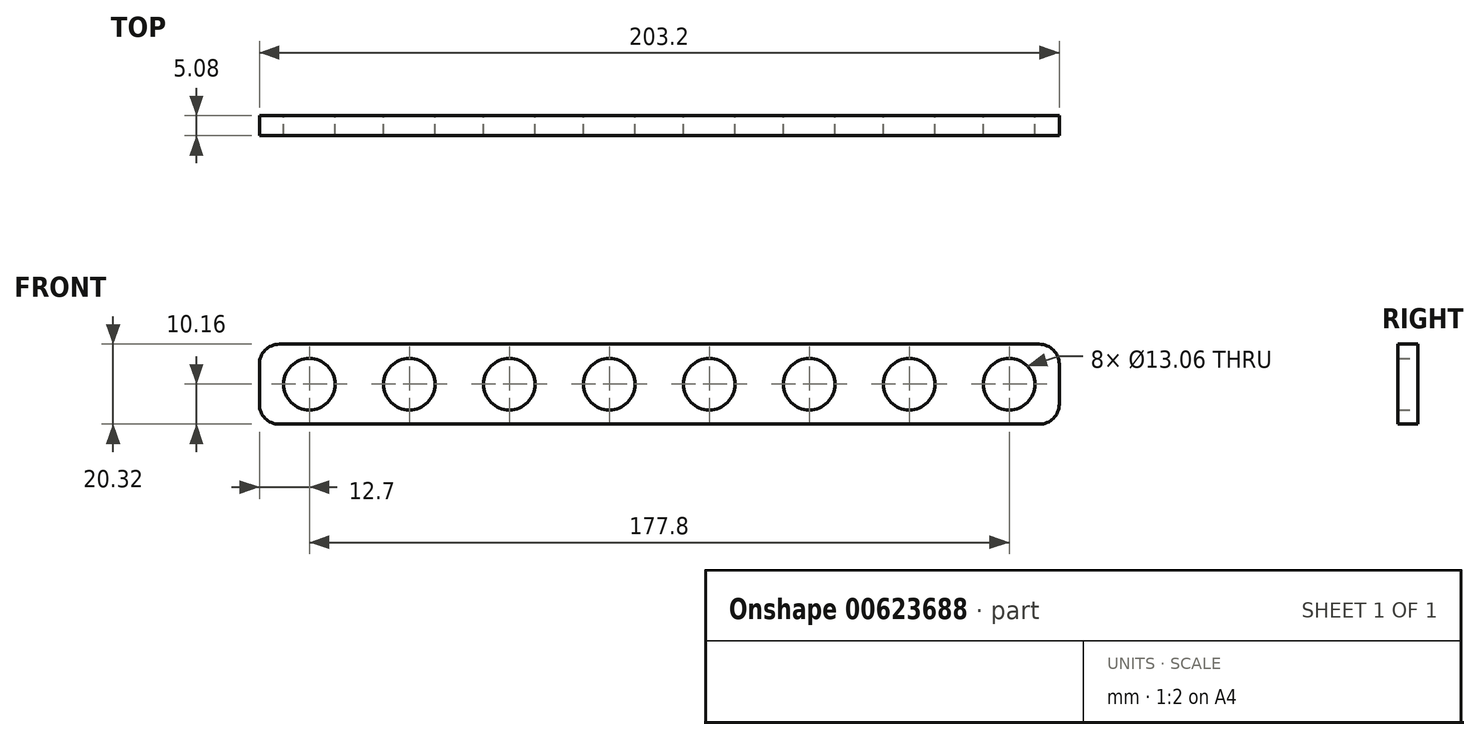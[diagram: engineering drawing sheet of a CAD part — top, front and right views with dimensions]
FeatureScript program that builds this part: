
annotation { "Feature Type Name" : "Feature", "Feature Type Description" : "" }
export const myFeature = defineFeature(function(context is Context, id is Id, definition is map)
    precondition{}
    {
        {
            var Q0;
            Q0=qCreatedBy(makeId("Front.planeOp"),FACE);
            var sketch = newSketch(context, id + "F0", { "sketchPlane" : qUnion([Q0])});
            skLineSegment(sketch, "E0", {"start": v(5.08, 0) * mm, "end": v(198.12, 0) * mm});
            skLineSegment(sketch, "E1", {"start": v(203.2, 5.08) * mm, "end": v(203.2, 15.24) * mm});
            skLineSegment(sketch, "E2", {"start": v(198.12, 20.32) * mm, "end": v(5.08, 20.32) * mm});
            skLineSegment(sketch, "E3", {"start": v(0, 15.24) * mm, "end": v(0, 5.08) * mm});
            skCircle(sketch, "E4", {"center": v(12.7, 10.16) * mm, "radius": 6.53 * mm});
            skPoint(sketch, "E4.centerSnap0", {"position": v(0, 10.16) * mm});
            skPoint(sketch, "E5.endSnap0", {"position": v(101.6, 20.32) * mm});
            skCircle(sketch, "E6.MirrorC", {"center": v(190.5, 10.16) * mm, "radius": 6.53 * mm});
            skPoint(sketch, "E7.visualSharp", {"position": v(0, 20.32) * mm});
            skArc(sketch, "E7.filletArc", {"start": v(5.08, 20.32) * mm, "mid": v(1.49, 18.83) * mm, "end": v(0, 15.24) * mm});
            skPoint(sketch, "E8.visualSharp", {"position": v(0, 0) * mm});
            skArc(sketch, "E8.filletArc", {"start": v(0, 5.08) * mm, "mid": v(1.49, 1.49) * mm, "end": v(5.08, 0) * mm});
            skPoint(sketch, "E9.visualSharp", {"position": v(203.2, 20.32) * mm});
            skArc(sketch, "E9.filletArc", {"start": v(203.2, 15.24) * mm, "mid": v(201.71, 18.83) * mm, "end": v(198.12, 20.32) * mm});
            skPoint(sketch, "E10.visualSharp", {"position": v(203.2, 0) * mm});
            skArc(sketch, "E10.filletArc", {"start": v(198.12, 0) * mm, "mid": v(201.71, 1.49) * mm, "end": v(203.2, 5.08) * mm});
            skCircle(sketch, "E11.1.0.0", {"center": v(38.1, 10.16) * mm, "radius": 6.53 * mm});
            skCircle(sketch, "E11.2.0.0", {"center": v(63.5, 10.16) * mm, "radius": 6.53 * mm});
            skCircle(sketch, "E11.3.0.0", {"center": v(88.9, 10.16) * mm, "radius": 6.53 * mm});
            skCircle(sketch, "E11.4.0.0", {"center": v(114.3, 10.16) * mm, "radius": 6.53 * mm});
            skCircle(sketch, "E11.5.0.0", {"center": v(139.7, 10.16) * mm, "radius": 6.53 * mm});
            skCircle(sketch, "E11.6.0.0", {"center": v(165.1, 10.16) * mm, "radius": 6.53 * mm});
            skLineSegment(sketch, "E11.direction1", {"start": v(12.7, 10.16) * mm, "end": v(38.1, 10.16) * mm, "construction": true});
            skSolve(sketch);
        }
        {
            var Q0;
            Q0 = qSketchRegion(id + "F0", true);
            extrude(context, id + "F1", {"entities" : qUnion([Q0]), "depth" : 5.08 * mm, "offsetDistance" : 25.4 * mm});
        }
    });
